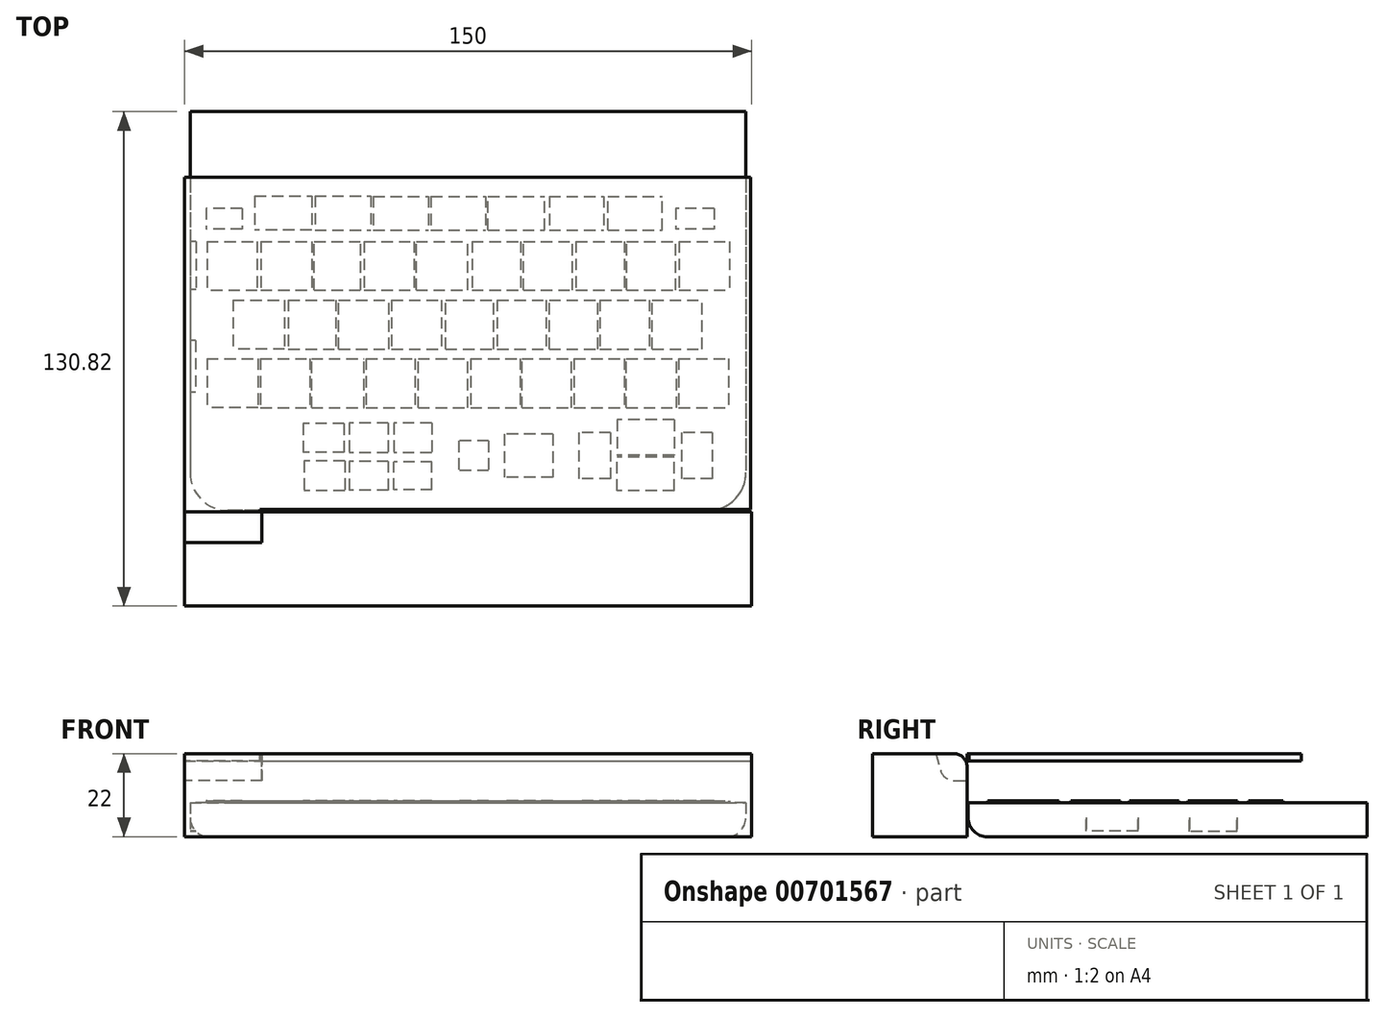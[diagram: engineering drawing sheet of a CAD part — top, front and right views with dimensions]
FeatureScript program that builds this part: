
annotation { "Feature Type Name" : "Feature", "Feature Type Description" : "" }
export const myFeature = defineFeature(function(context is Context, id is Id, definition is map)
    precondition{}
    {
        {
            var Q0;
            Q0=qCreatedBy(makeId("Top.planeOp"),FACE);
            var sketch = newSketch(context, id + "F0", { "sketchPlane" : qUnion([Q0])});
            skLineSegment(sketch, "E0.bottom", {"start": v(73.5, 56.32) * mm, "end": v(-73.5, 56.32) * mm});
            skLineSegment(sketch, "E0.top", {"start": v(63.5, -49.18) * mm, "end": v(-63.5, -49.18) * mm});
            skLineSegment(sketch, "E0.left", {"start": v(73.5, 56.32) * mm, "end": v(73.5, -39.18) * mm});
            skLineSegment(sketch, "E0.right", {"start": v(-73.5, 56.32) * mm, "end": v(-73.5, -39.18) * mm});
            skPoint(sketch, "E0.middle", {"position": v(0, 3.57) * mm});
            skPoint(sketch, "E1.visualSharp", {"position": v(-73.5, -49.18) * mm});
            skArc(sketch, "E1.filletArc", {"start": v(-73.5, -39.18) * mm, "mid": v(-70.57, -46.25) * mm, "end": v(-63.5, -49.18) * mm});
            skPoint(sketch, "E2.visualSharp", {"position": v(73.5, -49.18) * mm});
            skArc(sketch, "E2.filletArc", {"start": v(63.5, -49.18) * mm, "mid": v(70.57, -46.25) * mm, "end": v(73.5, -39.18) * mm});
            skSolve(sketch);
        }
        {
            var Q0;
            Q0=qCreatedBy(makeId("Top.planeOp"),FACE);
            var sketch = newSketch(context, id + "F1", { "sketchPlane" : qUnion([Q0])});
            skLineSegment(sketch, "E3.bottom", {"start": v(62.2, 6.5) * mm, "end": v(-62.2, 6.5) * mm});
            skLineSegment(sketch, "E3.top", {"start": v(62.2, -6.5) * mm, "end": v(-62.2, -6.5) * mm});
            skLineSegment(sketch, "E3.left", {"start": v(62.2, 6.5) * mm, "end": v(62.2, -6.5) * mm});
            skLineSegment(sketch, "E3.right", {"start": v(-62.2, 6.5) * mm, "end": v(-62.2, -6.5) * mm});
            skPoint(sketch, "E3.middle", {"position": v(0, 0) * mm});
            skLineSegment(sketch, "E4.bottom", {"start": v(69.04, 22) * mm, "end": v(-69.04, 22) * mm});
            skLineSegment(sketch, "E4.top", {"start": v(69.04, 9) * mm, "end": v(-69.04, 9) * mm});
            skLineSegment(sketch, "E4.left", {"start": v(69.04, 22) * mm, "end": v(69.04, 9) * mm});
            skLineSegment(sketch, "E4.right", {"start": v(-69.04, 22) * mm, "end": v(-69.04, 9) * mm});
            skPoint(sketch, "E4.middle", {"position": v(0, 15.5) * mm});
            skLineSegment(sketch, "E5.bottom", {"start": v(69.04, -9) * mm, "end": v(-69.04, -9) * mm});
            skLineSegment(sketch, "E5.top", {"start": v(69.04, -22) * mm, "end": v(-69.04, -22) * mm});
            skLineSegment(sketch, "E5.left", {"start": v(69.04, -9) * mm, "end": v(69.04, -22) * mm});
            skLineSegment(sketch, "E5.right", {"start": v(-69.04, -9) * mm, "end": v(-69.04, -22) * mm});
            skPoint(sketch, "E5.middle", {"position": v(0, -15.5) * mm});
            skLineSegment(sketch, "E6.bottom", {"start": v(-56.45, 34) * mm, "end": v(51.4, 34) * mm});
            skLineSegment(sketch, "E6.top", {"start": v(-56.45, 25) * mm, "end": v(51.4, 25) * mm});
            skLineSegment(sketch, "E6.left", {"start": v(-56.45, 34) * mm, "end": v(-56.45, 25) * mm});
            skLineSegment(sketch, "E6.right", {"start": v(51.4, 34) * mm, "end": v(51.4, 25) * mm});
            skLineSegment(sketch, "E7.bottom", {"start": v(-32.77, -26.18) * mm, "end": v(-43.57, -26.18) * mm});
            skLineSegment(sketch, "E7.top", {"start": v(-32.77, -33.82) * mm, "end": v(-43.57, -33.82) * mm});
            skLineSegment(sketch, "E7.left", {"start": v(-32.77, -26.18) * mm, "end": v(-32.77, -33.82) * mm});
            skLineSegment(sketch, "E7.right", {"start": v(-43.57, -26.18) * mm, "end": v(-43.57, -33.82) * mm});
            skPoint(sketch, "E7.middle", {"position": v(-38.17, -30) * mm});
            skLineSegment(sketch, "E8.bottom", {"start": v(-21.11, -26.08) * mm, "end": v(-31.49, -26.08) * mm});
            skLineSegment(sketch, "E8.top", {"start": v(-21.11, -33.92) * mm, "end": v(-31.49, -33.92) * mm});
            skLineSegment(sketch, "E8.left", {"start": v(-21.11, -26.08) * mm, "end": v(-21.11, -33.92) * mm});
            skLineSegment(sketch, "E8.right", {"start": v(-31.49, -26.08) * mm, "end": v(-31.49, -33.92) * mm});
            skPoint(sketch, "E8.middle", {"position": v(-26.3, -30) * mm});
            skLineSegment(sketch, "E9.bottom", {"start": v(-32.62, -36.1) * mm, "end": v(-43.38, -36.1) * mm});
            skLineSegment(sketch, "E9.top", {"start": v(-32.62, -43.9) * mm, "end": v(-43.38, -43.9) * mm});
            skLineSegment(sketch, "E9.left", {"start": v(-32.62, -36.1) * mm, "end": v(-32.62, -43.9) * mm});
            skLineSegment(sketch, "E9.right", {"start": v(-43.38, -36.1) * mm, "end": v(-43.38, -43.9) * mm});
            skPoint(sketch, "E9.middle", {"position": v(-38, -40) * mm});
            skLineSegment(sketch, "E10.bottom", {"start": v(-21.11, -36.2) * mm, "end": v(-31.49, -36.2) * mm});
            skLineSegment(sketch, "E10.top", {"start": v(-21.11, -43.8) * mm, "end": v(-31.49, -43.8) * mm});
            skLineSegment(sketch, "E10.left", {"start": v(-21.11, -36.2) * mm, "end": v(-21.11, -43.8) * mm});
            skLineSegment(sketch, "E10.right", {"start": v(-31.49, -36.2) * mm, "end": v(-31.49, -43.8) * mm});
            skPoint(sketch, "E10.middle", {"position": v(-26.3, -40) * mm});
            skLineSegment(sketch, "E11.bottom", {"start": v(-9.64, -26.08) * mm, "end": v(-19.56, -26.08) * mm});
            skLineSegment(sketch, "E11.top", {"start": v(-9.64, -33.92) * mm, "end": v(-19.56, -33.92) * mm});
            skLineSegment(sketch, "E11.left", {"start": v(-9.64, -26.08) * mm, "end": v(-9.64, -33.92) * mm});
            skLineSegment(sketch, "E11.right", {"start": v(-19.56, -26.08) * mm, "end": v(-19.56, -33.92) * mm});
            skPoint(sketch, "E11.middle", {"position": v(-14.6, -30) * mm});
            skLineSegment(sketch, "E12.bottom", {"start": v(-9.53, -43.69) * mm, "end": v(-19.67, -43.69) * mm});
            skLineSegment(sketch, "E12.top", {"start": v(-9.53, -36.31) * mm, "end": v(-19.67, -36.31) * mm});
            skLineSegment(sketch, "E12.left", {"start": v(-9.53, -43.69) * mm, "end": v(-9.53, -36.31) * mm});
            skLineSegment(sketch, "E12.right", {"start": v(-19.67, -43.69) * mm, "end": v(-19.67, -36.31) * mm});
            skPoint(sketch, "E12.middle", {"position": v(-14.6, -40) * mm});
            skLineSegment(sketch, "E13.bottom", {"start": v(5.43, -30.78) * mm, "end": v(-2.43, -30.78) * mm});
            skLineSegment(sketch, "E13.top", {"start": v(5.43, -38.62) * mm, "end": v(-2.43, -38.62) * mm});
            skLineSegment(sketch, "E13.left", {"start": v(5.43, -30.78) * mm, "end": v(5.43, -38.62) * mm});
            skLineSegment(sketch, "E13.right", {"start": v(-2.43, -30.78) * mm, "end": v(-2.43, -38.62) * mm});
            skPoint(sketch, "E13.middle", {"position": v(1.5, -34.7) * mm});
            skLineSegment(sketch, "E14.bottom", {"start": v(22.42, -29) * mm, "end": v(9.58, -29) * mm});
            skLineSegment(sketch, "E14.top", {"start": v(22.42, -40.4) * mm, "end": v(9.58, -40.4) * mm});
            skLineSegment(sketch, "E14.left", {"start": v(22.42, -29) * mm, "end": v(22.42, -40.4) * mm});
            skLineSegment(sketch, "E14.right", {"start": v(9.58, -29) * mm, "end": v(9.58, -40.4) * mm});
            skPoint(sketch, "E14.middle", {"position": v(16, -34.7) * mm});
            skLineSegment(sketch, "E15.bottom", {"start": v(54.57, -25.2) * mm, "end": v(39.43, -25.2) * mm});
            skLineSegment(sketch, "E15.top", {"start": v(54.57, -34.6) * mm, "end": v(39.43, -34.6) * mm});
            skLineSegment(sketch, "E15.left", {"start": v(54.57, -25.2) * mm, "end": v(54.57, -34.6) * mm});
            skLineSegment(sketch, "E15.right", {"start": v(39.43, -25.2) * mm, "end": v(39.43, -34.6) * mm});
            skPoint(sketch, "E15.middle", {"position": v(47, -29.9) * mm});
            skLineSegment(sketch, "E16.bottom", {"start": v(54.52, -43.98) * mm, "end": v(39.48, -43.98) * mm});
            skLineSegment(sketch, "E16.top", {"start": v(54.52, -35.02) * mm, "end": v(39.48, -35.02) * mm});
            skLineSegment(sketch, "E16.left", {"start": v(54.52, -43.98) * mm, "end": v(54.52, -35.02) * mm});
            skLineSegment(sketch, "E16.right", {"start": v(39.48, -43.98) * mm, "end": v(39.48, -35.02) * mm});
            skPoint(sketch, "E16.middle", {"position": v(47, -39.5) * mm});
            skLineSegment(sketch, "E17.bottom", {"start": v(37.71, -28.64) * mm, "end": v(29.29, -28.64) * mm});
            skLineSegment(sketch, "E17.top", {"start": v(37.71, -40.76) * mm, "end": v(29.29, -40.76) * mm});
            skLineSegment(sketch, "E17.left", {"start": v(37.71, -28.64) * mm, "end": v(37.71, -40.76) * mm});
            skLineSegment(sketch, "E17.right", {"start": v(29.29, -28.64) * mm, "end": v(29.29, -40.76) * mm});
            skPoint(sketch, "E17.middle", {"position": v(33.5, -34.7) * mm});
            skLineSegment(sketch, "E18.bottom", {"start": v(64.6, -28.57) * mm, "end": v(56.4, -28.57) * mm});
            skLineSegment(sketch, "E18.top", {"start": v(64.6, -40.83) * mm, "end": v(56.4, -40.83) * mm});
            skLineSegment(sketch, "E18.left", {"start": v(64.6, -28.57) * mm, "end": v(64.6, -40.83) * mm});
            skLineSegment(sketch, "E18.right", {"start": v(56.4, -28.57) * mm, "end": v(56.4, -40.83) * mm});
            skPoint(sketch, "E18.middle", {"position": v(60.5, -34.7) * mm});
            skLineSegment(sketch, "E19.bottom", {"start": v(-59.76, 30.75) * mm, "end": v(-69.24, 30.75) * mm});
            skLineSegment(sketch, "E19.top", {"start": v(-59.76, 25.25) * mm, "end": v(-69.24, 25.25) * mm});
            skLineSegment(sketch, "E19.left", {"start": v(-59.76, 30.75) * mm, "end": v(-59.76, 25.25) * mm});
            skLineSegment(sketch, "E19.right", {"start": v(-69.24, 30.75) * mm, "end": v(-69.24, 25.25) * mm});
            skPoint(sketch, "E19.middle", {"position": v(-64.5, 28) * mm});
            skLineSegment(sketch, "E20.bottom", {"start": v(65.06, 30.75) * mm, "end": v(54.94, 30.75) * mm});
            skLineSegment(sketch, "E20.top", {"start": v(65.06, 25.25) * mm, "end": v(54.94, 25.25) * mm});
            skLineSegment(sketch, "E20.left", {"start": v(65.06, 30.75) * mm, "end": v(65.06, 25.25) * mm});
            skLineSegment(sketch, "E20.right", {"start": v(54.94, 30.75) * mm, "end": v(54.94, 25.25) * mm});
            skPoint(sketch, "E20.middle", {"position": v(60, 28) * mm});
            skLineSegment(sketch, "E21", {"start": v(-38.17, -30) * mm, "end": v(-10.6, -30) * mm, "construction": true});
            skLineSegment(sketch, "E22", {"start": v(-38, -40) * mm, "end": v(-11.96, -40) * mm, "construction": true});
            skLineSegment(sketch, "E23", {"start": v(1.5, -34.7) * mm, "end": v(29.08, -34.7) * mm, "construction": true});
            skPoint(sketch, "E24", {"position": v(-9.53, -40) * mm});
            skLineSegment(sketch, "E25", {"start": v(47, -29.9) * mm, "end": v(47, -22.6) * mm, "construction": true});
            skPoint(sketch, "E26", {"position": v(0, 25) * mm});
            skLineSegment(sketch, "E27", {"start": v(0, 25) * mm, "end": v(0, 32.17) * mm, "construction": true});
            skPoint(sketch, "E28", {"position": v(51.4, 29.5) * mm});
            skLineSegment(sketch, "E29", {"start": v(51.4, 29.5) * mm, "end": v(-49.98, 29.5) * mm, "construction": true});
            skPoint(sketch, "E30", {"position": v(0, 29.5) * mm});
            skLineSegment(sketch, "E31", {"start": v(-26.3, -40) * mm, "end": v(-26.3, -37.32) * mm, "construction": true});
            skLineSegment(sketch, "E32", {"start": v(-14.6, -40) * mm, "end": v(-14.6, -37.32) * mm, "construction": true});
            skLineSegment(sketch, "E33", {"start": v(-55.16, 22) * mm, "end": v(-55.16, 9) * mm});
            skLineSegment(sketch, "E34", {"start": v(-41.36, 22) * mm, "end": v(-41.36, 9) * mm});
            skLineSegment(sketch, "E35", {"start": v(-41.15, 34) * mm, "end": v(-41.15, 25) * mm});
            skPoint(sketch, "E36", {"position": v(-48.8, 34) * mm});
            skLineSegment(sketch, "E37", {"start": v(-48.8, 34) * mm, "end": v(-48.8, 29.5) * mm, "construction": true});
            skSolve(sketch);
        }
        {
            var Q0;
            Q0 = qSketchRegion(id + "F0", true);
            extrude(context, id + "F2", {"entities" : qUnion([Q0]), "depth" : 9 * mm, "offsetDistance" : 25 * mm});
        }
        {
            var Q0;
            Q0=makeQuery(id+"F2.opExtrude","CAP_FACE",FACE,{"disambiguationData":[OSD([sQuery(id+"F0.wireOp",EDGE,"E0.bottom"),sQuery(id+"F0.wireOp",EDGE,"E0.top"),sQuery(id+"F0.wireOp",EDGE,"E0.left"),sQuery(id+"F0.wireOp",EDGE,"E0.right"),sQuery(id+"F0.wireOp",EDGE,"E1.filletArc"),sQuery(id+"F0.wireOp",EDGE,"E2.filletArc")])],"isStart":false});
            var sketch = newSketch(context, id + "F3", { "sketchPlane" : qUnion([Q0])});
            skLineSegment(sketch, "E38.0", {"start": v(-59.76, 30.75) * mm, "end": v(-69.24, 30.75) * mm});
            skLineSegment(sketch, "E38.1", {"start": v(-69.24, 30.75) * mm, "end": v(-69.24, 25.25) * mm});
            skLineSegment(sketch, "E38.2", {"start": v(-59.76, 25.25) * mm, "end": v(-69.24, 25.25) * mm});
            skLineSegment(sketch, "E38.3", {"start": v(-59.76, 30.75) * mm, "end": v(-59.76, 25.25) * mm});
            skLineSegment(sketch, "E38.4", {"start": v(65.06, 30.75) * mm, "end": v(65.06, 25.25) * mm});
            skLineSegment(sketch, "E38.5", {"start": v(65.06, 30.75) * mm, "end": v(54.94, 30.75) * mm});
            skLineSegment(sketch, "E38.6", {"start": v(54.94, 30.75) * mm, "end": v(54.94, 25.25) * mm});
            skLineSegment(sketch, "E38.7", {"start": v(65.06, 25.25) * mm, "end": v(54.94, 25.25) * mm});
            skLineSegment(sketch, "E38.8", {"start": v(-43.38, -36.1) * mm, "end": v(-43.38, -43.9) * mm});
            skLineSegment(sketch, "E38.9", {"start": v(-32.62, -36.1) * mm, "end": v(-32.62, -43.9) * mm});
            skLineSegment(sketch, "E38.10", {"start": v(-32.62, -36.1) * mm, "end": v(-43.38, -36.1) * mm});
            skLineSegment(sketch, "E38.11", {"start": v(-32.62, -43.9) * mm, "end": v(-43.38, -43.9) * mm});
            skLineSegment(sketch, "E39.0", {"start": v(64.6, -28.57) * mm, "end": v(64.6, -40.83) * mm});
            skLineSegment(sketch, "E39.1", {"start": v(64.6, -28.57) * mm, "end": v(56.4, -28.57) * mm});
            skLineSegment(sketch, "E39.2", {"start": v(64.6, -40.83) * mm, "end": v(56.4, -40.83) * mm});
            skLineSegment(sketch, "E39.3", {"start": v(56.4, -28.57) * mm, "end": v(56.4, -40.83) * mm});
            skLineSegment(sketch, "E39.4", {"start": v(54.52, -43.98) * mm, "end": v(54.52, -35.02) * mm});
            skLineSegment(sketch, "E39.5", {"start": v(54.52, -35.02) * mm, "end": v(39.48, -35.02) * mm});
            skLineSegment(sketch, "E39.6", {"start": v(39.48, -43.98) * mm, "end": v(39.48, -35.02) * mm});
            skLineSegment(sketch, "E39.7", {"start": v(54.52, -43.98) * mm, "end": v(39.48, -43.98) * mm});
            skLineSegment(sketch, "E40.2", {"start": v(-56.45, 34) * mm, "end": v(-56.45, 25) * mm});
            skLineSegment(sketch, "E41.1", {"start": v(-69.04, 22) * mm, "end": v(-69.04, 9) * mm});
            skLineSegment(sketch, "E41.4", {"start": v(-62.2, 6.5) * mm, "end": v(-62.2, -6.5) * mm});
            skLineSegment(sketch, "E42.0", {"start": v(-69.04, -9) * mm, "end": v(-69.04, -22) * mm});
            skLineSegment(sketch, "E43.0", {"start": v(-32.77, -26.18) * mm, "end": v(-32.77, -33.82) * mm});
            skLineSegment(sketch, "E43.1", {"start": v(-32.77, -26.18) * mm, "end": v(-43.57, -26.18) * mm});
            skLineSegment(sketch, "E43.2", {"start": v(-32.77, -33.82) * mm, "end": v(-43.57, -33.82) * mm});
            skLineSegment(sketch, "E43.3", {"start": v(-43.57, -26.18) * mm, "end": v(-43.57, -33.82) * mm});
            skLineSegment(sketch, "E44.0", {"start": v(-9.53, -43.69) * mm, "end": v(-19.67, -43.69) * mm});
            skLineSegment(sketch, "E44.1", {"start": v(-9.53, -43.69) * mm, "end": v(-9.53, -36.31) * mm});
            skLineSegment(sketch, "E44.2", {"start": v(-9.64, -26.08) * mm, "end": v(-9.64, -33.92) * mm});
            skLineSegment(sketch, "E44.3", {"start": v(-9.64, -26.08) * mm, "end": v(-19.56, -26.08) * mm});
            skLineSegment(sketch, "E44.4", {"start": v(-19.56, -26.08) * mm, "end": v(-19.56, -33.92) * mm});
            skLineSegment(sketch, "E44.5", {"start": v(-9.64, -33.92) * mm, "end": v(-19.56, -33.92) * mm});
            skLineSegment(sketch, "E44.6", {"start": v(-9.53, -36.31) * mm, "end": v(-19.67, -36.31) * mm});
            skLineSegment(sketch, "E44.7", {"start": v(-19.67, -43.69) * mm, "end": v(-19.67, -36.31) * mm});
            skLineSegment(sketch, "E45.0", {"start": v(-21.11, -43.8) * mm, "end": v(-31.49, -43.8) * mm});
            skLineSegment(sketch, "E45.1", {"start": v(-21.11, -36.2) * mm, "end": v(-21.11, -43.8) * mm});
            skLineSegment(sketch, "E45.2", {"start": v(-21.11, -33.92) * mm, "end": v(-31.49, -33.92) * mm});
            skLineSegment(sketch, "E45.3", {"start": v(-21.11, -26.08) * mm, "end": v(-21.11, -33.92) * mm});
            skLineSegment(sketch, "E45.4", {"start": v(-21.11, -26.08) * mm, "end": v(-31.49, -26.08) * mm});
            skLineSegment(sketch, "E45.5", {"start": v(-31.49, -26.08) * mm, "end": v(-31.49, -33.92) * mm});
            skLineSegment(sketch, "E45.6", {"start": v(-31.49, -36.2) * mm, "end": v(-31.49, -43.8) * mm});
            skLineSegment(sketch, "E45.7", {"start": v(-21.11, -36.2) * mm, "end": v(-31.49, -36.2) * mm});
            skLineSegment(sketch, "E46.0", {"start": v(5.43, -38.62) * mm, "end": v(-2.43, -38.62) * mm});
            skLineSegment(sketch, "E46.1", {"start": v(-2.43, -30.78) * mm, "end": v(-2.43, -38.62) * mm});
            skLineSegment(sketch, "E46.2", {"start": v(5.43, -30.78) * mm, "end": v(-2.43, -30.78) * mm});
            skLineSegment(sketch, "E46.3", {"start": v(5.43, -30.78) * mm, "end": v(5.43, -38.62) * mm});
            skLineSegment(sketch, "E46.4", {"start": v(22.42, -29) * mm, "end": v(9.58, -29) * mm});
            skLineSegment(sketch, "E46.5", {"start": v(9.58, -29) * mm, "end": v(9.58, -40.4) * mm});
            skLineSegment(sketch, "E46.6", {"start": v(22.42, -40.4) * mm, "end": v(9.58, -40.4) * mm});
            skLineSegment(sketch, "E46.7", {"start": v(22.42, -29) * mm, "end": v(22.42, -40.4) * mm});
            skLineSegment(sketch, "E46.8", {"start": v(29.29, -28.64) * mm, "end": v(29.29, -40.76) * mm});
            skLineSegment(sketch, "E46.9", {"start": v(37.71, -40.76) * mm, "end": v(29.29, -40.76) * mm});
            skLineSegment(sketch, "E46.10", {"start": v(37.71, -28.64) * mm, "end": v(29.29, -28.64) * mm});
            skLineSegment(sketch, "E46.11", {"start": v(37.71, -28.64) * mm, "end": v(37.71, -40.76) * mm});
            skLineSegment(sketch, "E47.0", {"start": v(39.43, -25.2) * mm, "end": v(39.43, -34.6) * mm});
            skLineSegment(sketch, "E47.1", {"start": v(54.57, -25.2) * mm, "end": v(39.43, -25.2) * mm});
            skLineSegment(sketch, "E47.2", {"start": v(54.57, -25.2) * mm, "end": v(54.57, -34.6) * mm});
            skLineSegment(sketch, "E47.3", {"start": v(54.57, -34.6) * mm, "end": v(39.43, -34.6) * mm});
            skLineSegment(sketch, "E48", {"start": v(-56.45, 34) * mm, "end": v(-41.32, 34) * mm});
            skLineSegment(sketch, "E49", {"start": v(-41.32, 34) * mm, "end": v(-41.32, 25) * mm});
            skLineSegment(sketch, "E50", {"start": v(-41.32, 25) * mm, "end": v(-56.45, 25) * mm});
            skLineSegment(sketch, "E51", {"start": v(-69.04, 22) * mm, "end": v(-55.76, 22) * mm});
            skLineSegment(sketch, "E52", {"start": v(-55.76, 22) * mm, "end": v(-55.76, 9) * mm});
            skLineSegment(sketch, "E53", {"start": v(-55.76, 9) * mm, "end": v(-69.04, 9) * mm});
            skLineSegment(sketch, "E54", {"start": v(-62.2, 6.5) * mm, "end": v(-48.54, 6.5) * mm});
            skLineSegment(sketch, "E55", {"start": v(-48.54, 6.5) * mm, "end": v(-48.54, -6.5) * mm});
            skLineSegment(sketch, "E56", {"start": v(-48.54, -6.5) * mm, "end": v(-62.2, -6.5) * mm});
            skLineSegment(sketch, "E57", {"start": v(-69.04, -9) * mm, "end": v(-55.56, -9) * mm});
            skLineSegment(sketch, "E58", {"start": v(-55.56, -9) * mm, "end": v(-55.56, -22) * mm});
            skLineSegment(sketch, "E59", {"start": v(-55.56, -22) * mm, "end": v(-69.04, -22) * mm});
            skLineSegment(sketch, "E60.bottom", {"start": v(-40.5, 34.07) * mm, "end": v(-25.72, 34.07) * mm});
            skLineSegment(sketch, "E60.top", {"start": v(-40.5, 25) * mm, "end": v(-25.72, 25) * mm});
            skLineSegment(sketch, "E60.left", {"start": v(-40.5, 34.07) * mm, "end": v(-40.5, 25) * mm});
            skLineSegment(sketch, "E60.right", {"start": v(-25.72, 34.07) * mm, "end": v(-25.72, 25) * mm});
            skLineSegment(sketch, "E61.bottom", {"start": v(-25.08, 33.91) * mm, "end": v(-10.41, 33.91) * mm});
            skLineSegment(sketch, "E61.top", {"start": v(-25.08, 25) * mm, "end": v(-10.41, 25) * mm});
            skLineSegment(sketch, "E61.left", {"start": v(-25.08, 33.91) * mm, "end": v(-25.08, 25) * mm});
            skLineSegment(sketch, "E61.right", {"start": v(-10.41, 33.91) * mm, "end": v(-10.41, 25) * mm});
            skLineSegment(sketch, "E62.bottom", {"start": v(-9.77, 33.91) * mm, "end": v(4.63, 33.91) * mm});
            skLineSegment(sketch, "E62.top", {"start": v(-9.77, 25) * mm, "end": v(4.63, 25) * mm});
            skLineSegment(sketch, "E62.left", {"start": v(-9.77, 33.91) * mm, "end": v(-9.77, 25) * mm});
            skLineSegment(sketch, "E62.right", {"start": v(4.63, 33.91) * mm, "end": v(4.63, 25) * mm});
            skLineSegment(sketch, "E63.bottom", {"start": v(5.32, 25) * mm, "end": v(20.31, 25) * mm});
            skLineSegment(sketch, "E63.top", {"start": v(5.32, 33.91) * mm, "end": v(20.31, 33.91) * mm});
            skLineSegment(sketch, "E63.left", {"start": v(5.32, 25) * mm, "end": v(5.32, 33.91) * mm});
            skLineSegment(sketch, "E63.right", {"start": v(20.31, 25) * mm, "end": v(20.31, 33.91) * mm});
            skLineSegment(sketch, "E64.bottom", {"start": v(21.48, 33.91) * mm, "end": v(35.94, 33.91) * mm});
            skLineSegment(sketch, "E64.top", {"start": v(21.48, 25) * mm, "end": v(35.94, 25) * mm});
            skLineSegment(sketch, "E64.left", {"start": v(21.48, 33.91) * mm, "end": v(21.48, 25) * mm});
            skLineSegment(sketch, "E64.right", {"start": v(35.94, 33.91) * mm, "end": v(35.94, 25) * mm});
            skLineSegment(sketch, "E65.bottom", {"start": v(37, 25) * mm, "end": v(51.35, 25) * mm});
            skLineSegment(sketch, "E65.top", {"start": v(37, 33.91) * mm, "end": v(51.35, 33.91) * mm});
            skLineSegment(sketch, "E65.left", {"start": v(37, 25) * mm, "end": v(37, 33.91) * mm});
            skLineSegment(sketch, "E65.right", {"start": v(51.35, 25) * mm, "end": v(51.35, 33.91) * mm});
            skLineSegment(sketch, "E66.bottom", {"start": v(-54.8, 22) * mm, "end": v(-41.32, 22) * mm});
            skLineSegment(sketch, "E66.top", {"start": v(-54.8, 9.1) * mm, "end": v(-41.32, 9.1) * mm});
            skLineSegment(sketch, "E66.left", {"start": v(-54.8, 22) * mm, "end": v(-54.8, 9.1) * mm});
            skLineSegment(sketch, "E66.right", {"start": v(-41.32, 22) * mm, "end": v(-41.32, 9.1) * mm});
            skLineSegment(sketch, "E67.bottom", {"start": v(-40.67, 9.1) * mm, "end": v(-28.36, 9.1) * mm});
            skLineSegment(sketch, "E67.top", {"start": v(-40.67, 22) * mm, "end": v(-28.36, 22) * mm});
            skLineSegment(sketch, "E67.left", {"start": v(-40.67, 9.1) * mm, "end": v(-40.67, 22) * mm});
            skLineSegment(sketch, "E67.right", {"start": v(-28.36, 9.1) * mm, "end": v(-28.36, 22) * mm});
            skLineSegment(sketch, "E68.bottom", {"start": v(-27.47, 22) * mm, "end": v(-14.34, 22) * mm});
            skLineSegment(sketch, "E68.top", {"start": v(-27.47, 9.1) * mm, "end": v(-14.34, 9.1) * mm});
            skLineSegment(sketch, "E68.left", {"start": v(-27.47, 22) * mm, "end": v(-27.47, 9.1) * mm});
            skLineSegment(sketch, "E68.right", {"start": v(-14.34, 22) * mm, "end": v(-14.34, 9.1) * mm});
            skLineSegment(sketch, "E69.bottom", {"start": v(-13.7, 9.1) * mm, "end": v(0, 9.1) * mm});
            skLineSegment(sketch, "E69.top", {"start": v(-13.7, 22) * mm, "end": v(0, 22) * mm});
            skLineSegment(sketch, "E69.left", {"start": v(-13.7, 9.1) * mm, "end": v(-13.7, 22) * mm});
            skLineSegment(sketch, "E69.right", {"start": v(0, 9.1) * mm, "end": v(0, 22) * mm});
            skLineSegment(sketch, "E70.bottom", {"start": v(1.07, 22) * mm, "end": v(13.88, 22) * mm});
            skLineSegment(sketch, "E70.top", {"start": v(1.07, 9.1) * mm, "end": v(13.88, 9.1) * mm});
            skLineSegment(sketch, "E70.left", {"start": v(1.07, 22) * mm, "end": v(1.07, 9.1) * mm});
            skLineSegment(sketch, "E70.right", {"start": v(13.88, 22) * mm, "end": v(13.88, 9.1) * mm});
            skLineSegment(sketch, "E71.bottom", {"start": v(14.7, 9.1) * mm, "end": v(27.58, 9.1) * mm});
            skLineSegment(sketch, "E71.top", {"start": v(14.7, 22) * mm, "end": v(27.58, 22) * mm});
            skLineSegment(sketch, "E71.left", {"start": v(14.7, 9.1) * mm, "end": v(14.7, 22) * mm});
            skLineSegment(sketch, "E71.right", {"start": v(27.58, 9.1) * mm, "end": v(27.58, 22) * mm});
            skLineSegment(sketch, "E72.bottom", {"start": v(28.54, 22) * mm, "end": v(41.35, 22) * mm});
            skLineSegment(sketch, "E72.top", {"start": v(28.54, 9.1) * mm, "end": v(41.35, 9.1) * mm});
            skLineSegment(sketch, "E72.left", {"start": v(28.54, 22) * mm, "end": v(28.54, 9.1) * mm});
            skLineSegment(sketch, "E72.right", {"start": v(41.35, 22) * mm, "end": v(41.35, 9.1) * mm});
            skLineSegment(sketch, "E73.bottom", {"start": v(41.98, 9.1) * mm, "end": v(54.98, 9.1) * mm});
            skLineSegment(sketch, "E73.top", {"start": v(41.98, 22) * mm, "end": v(54.98, 22) * mm});
            skLineSegment(sketch, "E73.left", {"start": v(41.98, 9.1) * mm, "end": v(41.98, 22) * mm});
            skLineSegment(sketch, "E73.right", {"start": v(54.98, 9.1) * mm, "end": v(54.98, 22) * mm});
            skLineSegment(sketch, "E74.bottom", {"start": v(55.87, 22) * mm, "end": v(69.13, 22) * mm});
            skLineSegment(sketch, "E74.top", {"start": v(55.87, 9.1) * mm, "end": v(69.13, 9.1) * mm});
            skLineSegment(sketch, "E74.left", {"start": v(55.87, 22) * mm, "end": v(55.87, 9.1) * mm});
            skLineSegment(sketch, "E74.right", {"start": v(69.13, 22) * mm, "end": v(69.13, 9.1) * mm});
            skLineSegment(sketch, "E75.bottom", {"start": v(-47.52, 6.5) * mm, "end": v(-34.97, 6.5) * mm});
            skLineSegment(sketch, "E75.top", {"start": v(-47.52, -6.5) * mm, "end": v(-34.97, -6.5) * mm});
            skLineSegment(sketch, "E75.left", {"start": v(-47.52, 6.5) * mm, "end": v(-47.52, -6.5) * mm});
            skLineSegment(sketch, "E75.right", {"start": v(-34.97, 6.5) * mm, "end": v(-34.97, -6.5) * mm});
            skLineSegment(sketch, "E76.bottom", {"start": v(-34.2, -6.5) * mm, "end": v(-20.88, -6.5) * mm});
            skLineSegment(sketch, "E76.top", {"start": v(-34.2, 6.5) * mm, "end": v(-20.88, 6.5) * mm});
            skLineSegment(sketch, "E76.left", {"start": v(-34.2, -6.5) * mm, "end": v(-34.2, 6.5) * mm});
            skLineSegment(sketch, "E76.right", {"start": v(-20.88, -6.5) * mm, "end": v(-20.88, 6.5) * mm});
            skLineSegment(sketch, "E77.bottom", {"start": v(-20.19, 6.5) * mm, "end": v(-7, 6.5) * mm});
            skLineSegment(sketch, "E77.top", {"start": v(-20.19, -6.5) * mm, "end": v(-7, -6.5) * mm});
            skLineSegment(sketch, "E77.left", {"start": v(-20.19, 6.5) * mm, "end": v(-20.19, -6.5) * mm});
            skLineSegment(sketch, "E77.right", {"start": v(-7, 6.5) * mm, "end": v(-7, -6.5) * mm});
            skLineSegment(sketch, "E78.bottom", {"start": v(-5.92, -6.5) * mm, "end": v(6.83, -6.5) * mm});
            skLineSegment(sketch, "E78.top", {"start": v(-5.92, 6.5) * mm, "end": v(6.83, 6.5) * mm});
            skLineSegment(sketch, "E78.left", {"start": v(-5.92, -6.5) * mm, "end": v(-5.92, 6.5) * mm});
            skLineSegment(sketch, "E78.right", {"start": v(6.83, -6.5) * mm, "end": v(6.83, 6.5) * mm});
            skLineSegment(sketch, "E79.bottom", {"start": v(7.72, 6.5) * mm, "end": v(20.6, 6.5) * mm});
            skLineSegment(sketch, "E79.top", {"start": v(7.72, -6.5) * mm, "end": v(20.6, -6.5) * mm});
            skLineSegment(sketch, "E79.left", {"start": v(7.72, 6.5) * mm, "end": v(7.72, -6.5) * mm});
            skLineSegment(sketch, "E79.right", {"start": v(20.6, 6.5) * mm, "end": v(20.6, -6.5) * mm});
            skLineSegment(sketch, "E80.bottom", {"start": v(21.49, -6.5) * mm, "end": v(34.3, -6.5) * mm});
            skLineSegment(sketch, "E80.top", {"start": v(21.49, 6.5) * mm, "end": v(34.3, 6.5) * mm});
            skLineSegment(sketch, "E80.left", {"start": v(21.49, -6.5) * mm, "end": v(21.49, 6.5) * mm});
            skLineSegment(sketch, "E80.right", {"start": v(34.3, -6.5) * mm, "end": v(34.3, 6.5) * mm});
            skLineSegment(sketch, "E81.bottom", {"start": v(34.87, 6.5) * mm, "end": v(48, 6.5) * mm});
            skLineSegment(sketch, "E81.top", {"start": v(34.87, -6.5) * mm, "end": v(48, -6.5) * mm});
            skLineSegment(sketch, "E81.left", {"start": v(34.87, 6.5) * mm, "end": v(34.87, -6.5) * mm});
            skLineSegment(sketch, "E81.right", {"start": v(48, 6.5) * mm, "end": v(48, -6.5) * mm});
            skLineSegment(sketch, "E82.bottom", {"start": v(48.76, -6.5) * mm, "end": v(61.89, -6.5) * mm});
            skLineSegment(sketch, "E82.top", {"start": v(48.76, 6.5) * mm, "end": v(61.89, 6.5) * mm});
            skLineSegment(sketch, "E82.left", {"start": v(48.76, -6.5) * mm, "end": v(48.76, 6.5) * mm});
            skLineSegment(sketch, "E82.right", {"start": v(61.89, -6.5) * mm, "end": v(61.89, 6.5) * mm});
            skLineSegment(sketch, "E83.bottom", {"start": v(-54.88, -9) * mm, "end": v(-41.83, -9) * mm});
            skLineSegment(sketch, "E83.top", {"start": v(-54.88, -22.01) * mm, "end": v(-41.83, -22.01) * mm});
            skLineSegment(sketch, "E83.left", {"start": v(-54.88, -9) * mm, "end": v(-54.88, -22.01) * mm});
            skLineSegment(sketch, "E83.right", {"start": v(-41.83, -9) * mm, "end": v(-41.83, -22.01) * mm});
            skLineSegment(sketch, "E84.bottom", {"start": v(-41.38, -22.01) * mm, "end": v(-27.53, -22.01) * mm});
            skLineSegment(sketch, "E84.top", {"start": v(-41.38, -9) * mm, "end": v(-27.53, -9) * mm});
            skLineSegment(sketch, "E84.left", {"start": v(-41.38, -22.01) * mm, "end": v(-41.38, -9) * mm});
            skLineSegment(sketch, "E84.right", {"start": v(-27.53, -22.01) * mm, "end": v(-27.53, -9) * mm});
            skLineSegment(sketch, "E85.bottom", {"start": v(-26.99, -9) * mm, "end": v(-13.98, -9) * mm});
            skLineSegment(sketch, "E85.top", {"start": v(-26.99, -22.01) * mm, "end": v(-13.98, -22.01) * mm});
            skLineSegment(sketch, "E85.left", {"start": v(-26.99, -9) * mm, "end": v(-26.99, -22.01) * mm});
            skLineSegment(sketch, "E85.right", {"start": v(-13.98, -9) * mm, "end": v(-13.98, -22.01) * mm});
            skLineSegment(sketch, "E86.bottom", {"start": v(-13.17, -22.01) * mm, "end": v(0, -22.01) * mm});
            skLineSegment(sketch, "E86.top", {"start": v(-13.17, -9) * mm, "end": v(0, -9) * mm});
            skLineSegment(sketch, "E86.left", {"start": v(-13.17, -22.01) * mm, "end": v(-13.17, -9) * mm});
            skLineSegment(sketch, "E86.right", {"start": v(0, -22.01) * mm, "end": v(0, -9) * mm});
            skLineSegment(sketch, "E87.bottom", {"start": v(0.69, -9) * mm, "end": v(13.74, -9) * mm});
            skLineSegment(sketch, "E87.top", {"start": v(0.69, -22.01) * mm, "end": v(13.74, -22.01) * mm});
            skLineSegment(sketch, "E87.left", {"start": v(0.69, -9) * mm, "end": v(0.69, -22.01) * mm});
            skLineSegment(sketch, "E87.right", {"start": v(13.74, -9) * mm, "end": v(13.74, -22.01) * mm});
            skLineSegment(sketch, "E88.bottom", {"start": v(14.23, -22.01) * mm, "end": v(27.42, -22.01) * mm});
            skLineSegment(sketch, "E88.top", {"start": v(14.23, -9) * mm, "end": v(27.42, -9) * mm});
            skLineSegment(sketch, "E88.left", {"start": v(14.23, -22.01) * mm, "end": v(14.23, -9) * mm});
            skLineSegment(sketch, "E88.right", {"start": v(27.42, -22.01) * mm, "end": v(27.42, -9) * mm});
            skLineSegment(sketch, "E89.bottom", {"start": v(28, -9) * mm, "end": v(41.32, -9) * mm});
            skLineSegment(sketch, "E89.top", {"start": v(28, -22.01) * mm, "end": v(41.32, -22.01) * mm});
            skLineSegment(sketch, "E89.left", {"start": v(28, -9) * mm, "end": v(28, -22.01) * mm});
            skLineSegment(sketch, "E89.right", {"start": v(41.32, -9) * mm, "end": v(41.32, -22.01) * mm});
            skLineSegment(sketch, "E90.bottom", {"start": v(41.9, -22.01) * mm, "end": v(55.22, -22.01) * mm});
            skLineSegment(sketch, "E90.top", {"start": v(41.9, -9) * mm, "end": v(55.22, -9) * mm});
            skLineSegment(sketch, "E90.left", {"start": v(41.9, -22.01) * mm, "end": v(41.9, -9) * mm});
            skLineSegment(sketch, "E90.right", {"start": v(55.22, -22.01) * mm, "end": v(55.22, -9) * mm});
            skLineSegment(sketch, "E91.bottom", {"start": v(55.76, -9) * mm, "end": v(68.9, -9) * mm});
            skLineSegment(sketch, "E91.top", {"start": v(55.76, -22.01) * mm, "end": v(68.9, -22.01) * mm});
            skLineSegment(sketch, "E91.left", {"start": v(55.76, -9) * mm, "end": v(55.76, -22.01) * mm});
            skLineSegment(sketch, "E91.right", {"start": v(68.9, -9) * mm, "end": v(68.9, -22.01) * mm});
            skSolve(sketch);
        }
        {
            var Q0;
            Q0 = qSketchRegion(id + "F3", true);
            extrude(context, id + "F4", {"entities" : qUnion([Q0]), "operationType" : NewBodyOperationType.ADD, "depth" : 0.5 * mm, "offsetDistance" : 25 * mm});
        }
        {
            var Q0;
            Q0=makeQuery(id+"F2.opExtrude","CAP_EDGE",EDGE,{"disambiguationData":[OSD([sQuery(id+"F0.wireOp",EDGE,"E0.right")])],"isStart":true});
            fillet(context, id + "F5", {"entities" : qUnion([Q0]), "radius" : 5 * mm, "tangentPropagation" : true, "allowEdgeOverflow" : false});
        }
        {
            var Q0;
            Q0=makeQuery(id+"F2.opExtrude","SWEPT_FACE",FACE,{"disambiguationData":[OSD([sQuery(id+"F0.wireOp",EDGE,"E0.right")])]});
            var sketch = newSketch(context, id + "F6", { "sketchPlane" : qUnion([Q0])});
            skLineSegment(sketch, "E92.bottom", {"start": v(-21.92, 6.94) * mm, "end": v(-9.28, 6.94) * mm});
            skLineSegment(sketch, "E92.top", {"start": v(-21.92, 1.37) * mm, "end": v(-9.28, 1.37) * mm});
            skLineSegment(sketch, "E92.left", {"start": v(-21.92, 6.94) * mm, "end": v(-21.92, 1.37) * mm});
            skLineSegment(sketch, "E92.right", {"start": v(-9.28, 6.94) * mm, "end": v(-9.28, 1.37) * mm});
            skLineSegment(sketch, "E93.bottom", {"start": v(4.26, 7.58) * mm, "end": v(17.97, 7.58) * mm});
            skLineSegment(sketch, "E93.top", {"start": v(4.26, 1.51) * mm, "end": v(17.97, 1.51) * mm});
            skLineSegment(sketch, "E93.left", {"start": v(4.26, 7.58) * mm, "end": v(4.26, 1.51) * mm});
            skLineSegment(sketch, "E93.right", {"start": v(17.97, 7.58) * mm, "end": v(17.97, 1.51) * mm});
            skSolve(sketch);
        }
        {
            var Q0;
            Q0 = qSketchRegion(id + "F6", true);
            extrude(context, id + "F7", {"entities" : qUnion([Q0]), "operationType" : NewBodyOperationType.ADD, "oppositeDirection" : true, "depth" : 25 * mm, "offsetDistance" : 25 * mm});
        }
        {
            var Q0;
            Q0=qCreatedBy(makeId("Top.planeOp"),FACE);
            var sketch = newSketch(context, id + "F8", { "sketchPlane" : qUnion([Q0])});
            skLineSegment(sketch, "E94.bottom", {"start": v(75, -49.5) * mm, "end": v(-75, -49.5) * mm});
            skLineSegment(sketch, "E94.top", {"start": v(75, -74.5) * mm, "end": v(-75, -74.5) * mm});
            skLineSegment(sketch, "E94.left", {"start": v(75, -49.5) * mm, "end": v(75, -74.5) * mm});
            skLineSegment(sketch, "E94.right", {"start": v(-75, -49.5) * mm, "end": v(-75, -74.5) * mm});
            skPoint(sketch, "E94.middle", {"position": v(0, -62) * mm});
            skSolve(sketch);
        }
        {
            var Q0;
            Q0 = qSketchRegion(id + "F8", true);
            extrude(context, id + "F9", {"entities" : qUnion([Q0]), "depth" : 22 * mm, "offsetDistance" : 25 * mm});
        }
        {
            var Q0;
            Q0=qCreatedBy(makeId("Top.planeOp"),FACE);
            cPlane(context, id + "F10", {"entities" : qUnion([Q0]), "cplaneType" : CPlaneType.OFFSET, "offset" : 20 * mm, "width" : 150 * mm, "height" : 150 * mm});
        }
        {
            var Q0;
            Q0=qCreatedBy(id+"F10.planeOp",FACE);
            var sketch = newSketch(context, id + "F11", { "sketchPlane" : qUnion([Q0])});
            skLineSegment(sketch, "E95.bottom", {"start": v(-75, 38.9) * mm, "end": v(74.77, 38.9) * mm});
            skLineSegment(sketch, "E95.top", {"start": v(-75, -48.93) * mm, "end": v(74.77, -48.93) * mm});
            skLineSegment(sketch, "E95.left", {"start": v(-75, 38.9) * mm, "end": v(-75, -48.93) * mm});
            skLineSegment(sketch, "E95.right", {"start": v(74.77, 38.9) * mm, "end": v(74.77, -48.93) * mm});
            skSolve(sketch);
        }
        {
            var Q0;
            Q0 = qSketchRegion(id + "F11", true);
            extrude(context, id + "F12", {"entities" : qUnion([Q0]), "depth" : 2 * mm, "offsetDistance" : 25 * mm});
        }
        {
            var Q0;
            Q0=makeQuery(id+"F12.opExtrude","CAP_FACE",FACE,{"disambiguationData":[OSD([sQuery(id+"F11.wireOp",EDGE,"E95.bottom"),sQuery(id+"F11.wireOp",EDGE,"E95.top"),sQuery(id+"F11.wireOp",EDGE,"E95.left"),sQuery(id+"F11.wireOp",EDGE,"E95.right")])],"isStart":false});
            var sketch = newSketch(context, id + "F13", { "sketchPlane" : qUnion([Q0])});
            skLineSegment(sketch, "E96.bottom", {"start": v(-75, -48.93) * mm, "end": v(-55, -48.93) * mm});
            skLineSegment(sketch, "E96.top", {"start": v(-75, -58.93) * mm, "end": v(-55, -58.93) * mm});
            skLineSegment(sketch, "E96.left", {"start": v(-75, -48.93) * mm, "end": v(-75, -58.93) * mm});
            skLineSegment(sketch, "E96.right", {"start": v(-55, -48.93) * mm, "end": v(-55, -58.93) * mm});
            skSolve(sketch);
        }
        {
            var Q0;
            Q0=qCreatedBy(makeId("Right.planeOp"),FACE);
            var Q1;
            Q1=sQuery(id+"F13.wireOp",VERTEX,"E96.left.start");
            cPlane(context, id + "F14", {"entities" : qUnion([Q0, Q1]), "cplaneType" : CPlaneType.PLANE_POINT, "offset" : 25 * mm, "width" : 150 * mm, "height" : 150 * mm});
        }
        {
            var Q0;
            Q0=qCreatedBy(id+"F14.planeOp",FACE);
            var sketch = newSketch(context, id + "F15", { "sketchPlane" : qUnion([Q0])});
            skCircle(sketch, "E97", {"center": v(-53.03, 18.47) * mm, "radius": 1.52 * mm});
            skCircle(sketch, "E98.0", {"center": v(-53.03, 18.47) * mm, "radius": 3.52 * mm});
            skLineSegment(sketch, "E99", {"start": v(-48.93, 22) * mm, "end": v(-53.03, 22) * mm});
            skLineSegment(sketch, "E100", {"start": v(-53.03, 22) * mm, "end": v(-53.03, 20) * mm});
            skLineSegment(sketch, "E101", {"start": v(-53.03, 20) * mm, "end": v(-48.93, 20) * mm});
            skLineSegment(sketch, "E102", {"start": v(-48.93, 20) * mm, "end": v(-48.93, 22) * mm});
            skLineSegment(sketch, "E103", {"start": v(-53.03, 18.47) * mm, "end": v(-53.03, 19.31) * mm, "construction": true});
            skLineSegment(sketch, "E104", {"start": v(-49.5, 18.47) * mm, "end": v(-49.5, 20) * mm});
            skLineSegment(sketch, "E105", {"start": v(-53.03, 18.47) * mm, "end": v(-52.05, 18.47) * mm, "construction": true});
            skSolve(sketch);
        }
        {
            var Q0;
            Q0 = qSketchRegion(id + "F15", true);
            extrude(context, id + "F16", {"entities" : qUnion([Q0]), "operationType" : NewBodyOperationType.ADD, "depth" : 20 * mm, "offsetDistance" : 25 * mm});
        }
        {
            var Q0;
            Q0=qCreatedBy(id+"F14.planeOp",FACE);
            var sketch = newSketch(context, id + "F17", { "sketchPlane" : qUnion([Q0])});
            skCircle(sketch, "E106.0", {"center": v(-53.03, 18.47) * mm, "radius": 1.52 * mm});
            skSolve(sketch);
        }
        {
            var Q0;
            Q0 = qSketchRegion(id + "F17", true);
            extrude(context, id + "F18", {"entities" : qUnion([Q0]), "operationType" : NewBodyOperationType.ADD, "depth" : 2 * mm, "offsetDistance" : 25 * mm});
        }
        {
            var Q0;
            Q0=qCreatedBy(id+"F14.planeOp",FACE);
            var sketch = newSketch(context, id + "F19", { "sketchPlane" : qUnion([Q0])});
            skArc(sketch, "E107", {"start": v(-56.5, 17.54) * mm, "mid": v(-55.22, 15.62) * mm, "end": v(-53.03, 14.88) * mm});
            skLineSegment(sketch, "E108", {"start": v(-53.03, 14.87) * mm, "end": v(-49.5, 14.87) * mm});
            skLineSegment(sketch, "E109", {"start": v(-49.5, 14.87) * mm, "end": v(-49.5, 22) * mm});
            skLineSegment(sketch, "E110", {"start": v(-49.5, 22) * mm, "end": v(-57.7, 22) * mm});
            skLineSegment(sketch, "E111", {"start": v(-57.7, 22) * mm, "end": v(-56.5, 17.54) * mm});
            skLineSegment(sketch, "E112", {"start": v(-53.03, 18.47) * mm, "end": v(-55.93, 18.47) * mm, "construction": true});
            skLineSegment(sketch, "E113", {"start": v(-53.03, 18.47) * mm, "end": v(-53.03, 15.59) * mm, "construction": true});
            skSolve(sketch);
        }
        {
            var Q0;
            Q0 = qSketchRegion(id + "F19", true);
            extrude(context, id + "F20", {"entities" : qUnion([Q0]), "operationType" : NewBodyOperationType.REMOVE, "depth" : 20.5 * mm, "offsetDistance" : 25 * mm});
        }
        {
            var Q0;
            Q0=makeQuery(id+"F9.opExtrude","CAP_EDGE",EDGE,{"disambiguationData":[OSD([sQuery(id+"F8.wireOp",EDGE,"E94.bottom")])],"isStart":false});
            fillet(context, id + "F21", {"entities" : qUnion([Q0]), "radius" : 3.5 * mm, "tangentPropagation" : true, "allowEdgeOverflow" : false});
        }
    });
